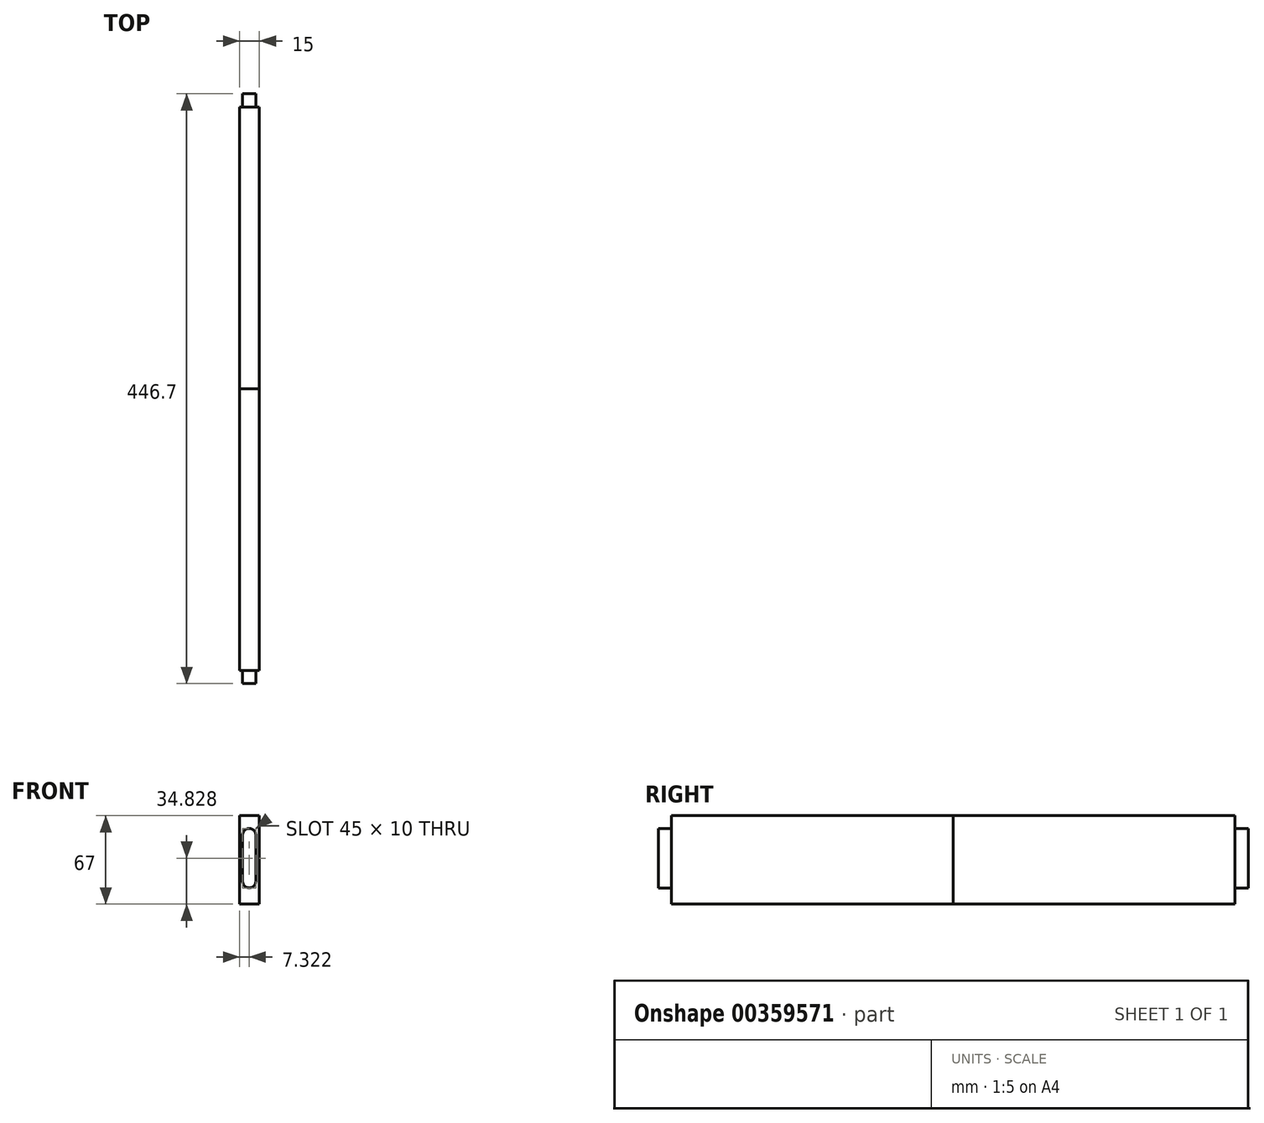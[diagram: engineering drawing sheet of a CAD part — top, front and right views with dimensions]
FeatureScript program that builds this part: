
annotation { "Feature Type Name" : "Feature", "Feature Type Description" : "" }
export const myFeature = defineFeature(function(context is Context, id is Id, definition is map)
    precondition{}
    {
        {
            var Q0;
            Q0=qCreatedBy(makeId("Right.planeOp"),FACE);
            var sketch = newSketch(context, id + "F0", { "sketchPlane" : qUnion([Q0])});
            skLineSegment(sketch, "E0.bottom", {"start": v(-213.35, 41.51) * mm, "end": v(0, 41.51) * mm});
            skLineSegment(sketch, "E0.top", {"start": v(-213.35, -25.49) * mm, "end": v(0, -25.49) * mm});
            skLineSegment(sketch, "E0.left", {"start": v(-213.35, 41.51) * mm, "end": v(-213.35, -25.49) * mm});
            skLineSegment(sketch, "E0.right", {"start": v(0, 41.51) * mm, "end": v(0, -25.49) * mm});
            skSolve(sketch);
        }
        {
            var Q0;
            Q0 = qSketchRegion(id + "F0", true);
            extrude(context, id + "F1", {"entities" : qUnion([Q0]), "depth" : 15 * mm});
        }
        {
            var Q0;
            Q0=makeQuery(id+"F1.opExtrude","SWEPT_FACE",FACE,{"disambiguationData":[OSD([sQuery(id+"F0.wireOp",EDGE,"E0.left")])]});
            var sketch = newSketch(context, id + "F2", { "sketchPlane" : qUnion([Q0])});
            skLineSegment(sketch, "E1.bottom", {"start": v(2.32, 31.84) * mm, "end": v(12.32, 31.84) * mm});
            skLineSegment(sketch, "E1.top", {"start": v(2.32, -13.16) * mm, "end": v(12.32, -13.16) * mm});
            skLineSegment(sketch, "E1.left", {"start": v(2.32, 31.84) * mm, "end": v(2.32, -13.16) * mm});
            skLineSegment(sketch, "E1.right", {"start": v(12.32, 31.84) * mm, "end": v(12.32, -13.16) * mm});
            skSolve(sketch);
        }
        {
            var Q0;
            Q0 = qSketchRegion(id + "F2", true);
            extrude(context, id + "F3", {"entities" : qUnion([Q0]), "operationType" : NewBodyOperationType.ADD, "depth" : 10 * mm});
        }
        {
            var Q0;
            Q0=makeQuery(id+"F3.opExtrude","SWEPT_EDGE",EDGE,{"disambiguationData":[OSD([sQuery(id+"F2.wireOp",EDGE,"E1.bottom"),sQuery(id+"F2.wireOp",EDGE,"E1.right")])]});
            var Q1;
            Q1=makeQuery(id+"F3.opExtrude","SWEPT_EDGE",EDGE,{"disambiguationData":[OSD([sQuery(id+"F2.wireOp",EDGE,"E1.bottom"),sQuery(id+"F2.wireOp",EDGE,"E1.left")])]});
            var Q2;
            Q2=makeQuery(id+"F3.opExtrude","SWEPT_EDGE",EDGE,{"disambiguationData":[OSD([sQuery(id+"F2.wireOp",EDGE,"E1.top"),sQuery(id+"F2.wireOp",EDGE,"E1.left")])]});
            var Q3;
            Q3=makeQuery(id+"F3.opExtrude","SWEPT_EDGE",EDGE,{"disambiguationData":[OSD([sQuery(id+"F2.wireOp",EDGE,"E1.top"),sQuery(id+"F2.wireOp",EDGE,"E1.right")])]});
            fillet(context, id + "F4", {"entities" : qUnion([Q0, Q1, Q2, Q3]), "radius" : 5 * mm, "tangentPropagation" : true, "allowEdgeOverflow" : false});
        }
        {
            var Q0;
            Q0=makeQuery(id+"F1.opExtrude","SWEPT_BODY",BODY,{"disambiguationData":[OSD([sQuery(id+"F0.wireOp",EDGE,"E0.bottom"),sQuery(id+"F0.wireOp",EDGE,"E0.top"),sQuery(id+"F0.wireOp",EDGE,"E0.left"),sQuery(id+"F0.wireOp",EDGE,"E0.right")])]});
            var Q1;
            Q1=qCreatedBy(makeId("Front.planeOp"),FACE);
            mirror(context, id + "F5", {"entities" : qUnion([Q0]), "mirrorPlane" : qUnion([Q1])});
        }
    });
